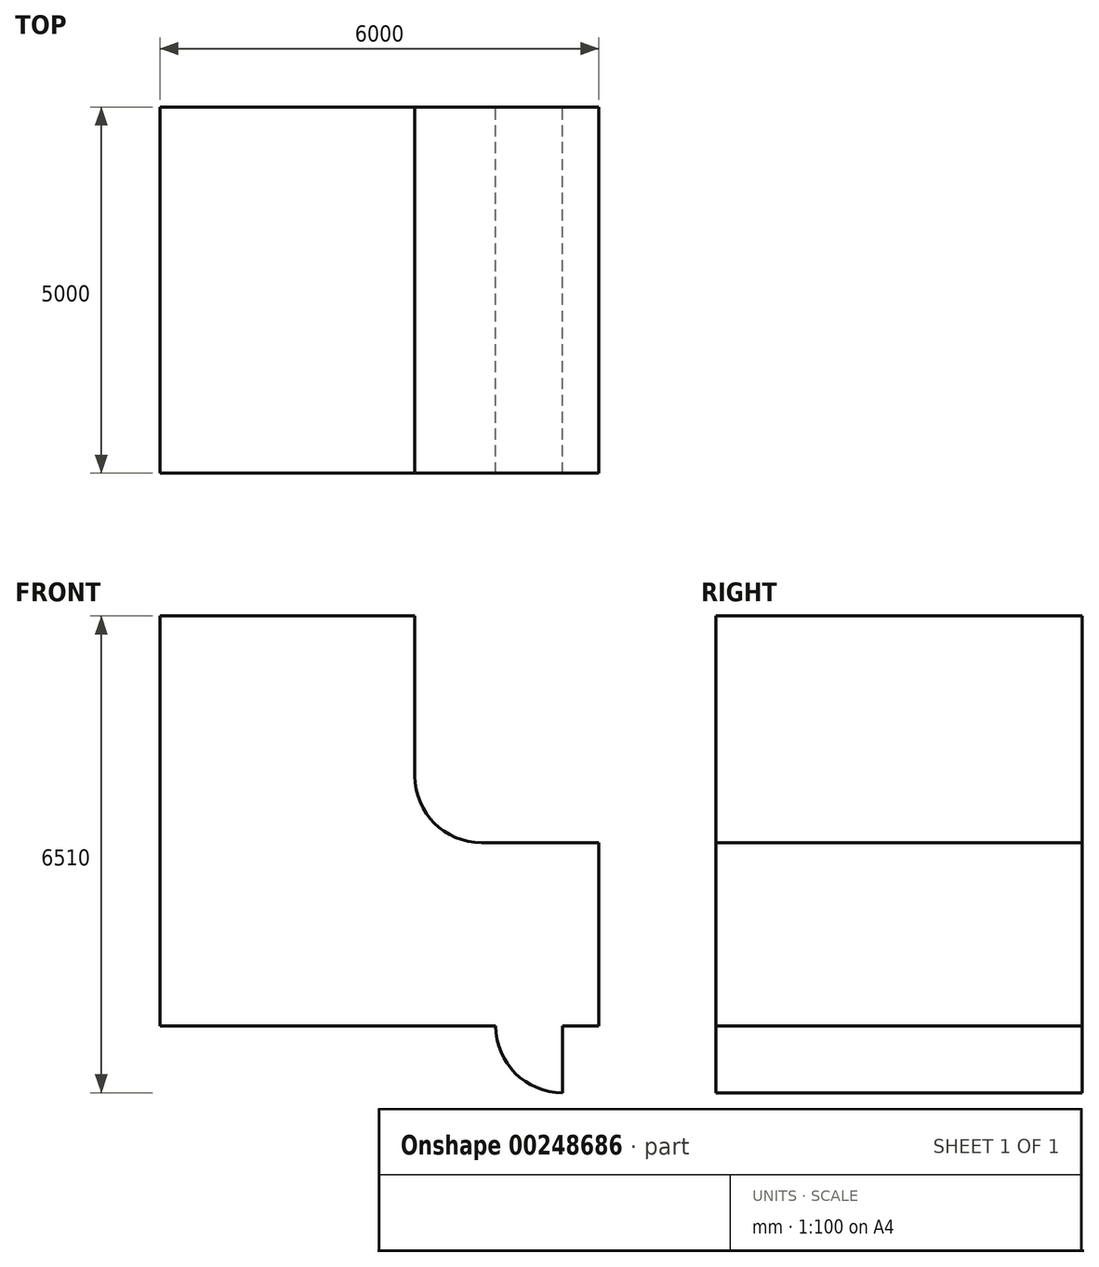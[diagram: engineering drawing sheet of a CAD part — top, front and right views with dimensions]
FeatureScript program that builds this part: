
annotation { "Feature Type Name" : "Feature", "Feature Type Description" : "" }
export const myFeature = defineFeature(function(context is Context, id is Id, definition is map)
    precondition{}
    {
        {
            var Q0;
            Q0=qCreatedBy(makeId("Front.planeOp"),FACE);
            var sketch = newSketch(context, id + "F0", { "sketchPlane" : qUnion([Q0])});
            skLineSegment(sketch, "E0", {"start": v(0, 5600) * mm, "end": v(0, 0) * mm});
            skLineSegment(sketch, "E1", {"start": v(0, 0) * mm, "end": v(4590, 0) * mm});
            skLineSegment(sketch, "E2", {"start": v(5500, 0) * mm, "end": v(6000, 0) * mm});
            skLineSegment(sketch, "E3", {"start": v(6000, 0) * mm, "end": v(6000, 2505) * mm});
            skLineSegment(sketch, "E4", {"start": v(0, 5600) * mm, "end": v(3485, 5600) * mm});
            skPoint(sketch, "E5.visualSharp", {"position": v(3485, 2505) * mm});
            skLineSegment(sketch, "E6", {"start": v(3485, 5600) * mm, "end": v(4385, 5600) * mm});
            skLineSegment(sketch, "E7", {"start": v(3485, 5600) * mm, "end": v(3485, 3415) * mm});
            skLineSegment(sketch, "E8", {"start": v(4395, 2505) * mm, "end": v(6000, 2505) * mm});
            skLineSegment(sketch, "E9", {"start": v(3935, 5600) * mm, "end": v(3935, 3410) * mm});
            skLineSegment(sketch, "E10", {"start": v(4385, 5600) * mm, "end": v(4385, 3405) * mm});
            skLineSegment(sketch, "E11", {"start": v(4390, 2955) * mm, "end": v(6000, 2955) * mm});
            skLineSegment(sketch, "E12", {"start": v(4385, 3405) * mm, "end": v(6000, 3405) * mm});
            skLineSegment(sketch, "E13", {"start": v(6000, 3405) * mm, "end": v(6000, 2505) * mm});
            skLineSegment(sketch, "E14", {"start": v(3485, 5600) * mm, "end": v(3485, 5310) * mm});
            skLineSegment(sketch, "E15", {"start": v(3485, 5310) * mm, "end": v(3485, 5020) * mm});
            skLineSegment(sketch, "E16", {"start": v(3485, 5020) * mm, "end": v(3485, 4730) * mm});
            skLineSegment(sketch, "E17", {"start": v(3485, 4730) * mm, "end": v(3485, 4440) * mm});
            skLineSegment(sketch, "E18", {"start": v(3485, 4440) * mm, "end": v(3485, 4150) * mm});
            skLineSegment(sketch, "E19", {"start": v(3485, 4150) * mm, "end": v(3485, 3860) * mm});
            skLineSegment(sketch, "E20", {"start": v(3485, 3860) * mm, "end": v(4385, 3860) * mm});
            skLineSegment(sketch, "E21", {"start": v(3485, 4150) * mm, "end": v(4385, 4150) * mm});
            skLineSegment(sketch, "E22", {"start": v(3485, 4440) * mm, "end": v(4385, 4440) * mm});
            skLineSegment(sketch, "E23", {"start": v(4385, 4440) * mm, "end": v(4385, 4150) * mm});
            skLineSegment(sketch, "E24", {"start": v(4385, 3860) * mm, "end": v(4385, 4150) * mm});
            skLineSegment(sketch, "E25", {"start": v(3485, 4730) * mm, "end": v(4385, 4730) * mm});
            skLineSegment(sketch, "E26", {"start": v(4385, 4730) * mm, "end": v(4385, 4440) * mm});
            skLineSegment(sketch, "E27", {"start": v(3485, 5020) * mm, "end": v(4385, 5020) * mm});
            skLineSegment(sketch, "E28", {"start": v(4385, 5020) * mm, "end": v(4385, 4730) * mm});
            skLineSegment(sketch, "E29", {"start": v(3485, 5310) * mm, "end": v(4385, 5310) * mm});
            skLineSegment(sketch, "E30", {"start": v(4385, 5310) * mm, "end": v(4385, 5020) * mm});
            skLineSegment(sketch, "E31", {"start": v(4385, 5600) * mm, "end": v(4385, 5310) * mm});
            skLineSegment(sketch, "E32", {"start": v(6000, 2505) * mm, "end": v(5710, 2505) * mm});
            skLineSegment(sketch, "E33", {"start": v(5710, 2505) * mm, "end": v(5420, 2505) * mm});
            skLineSegment(sketch, "E34", {"start": v(5420, 2505) * mm, "end": v(5130, 2505) * mm});
            skLineSegment(sketch, "E35", {"start": v(5130, 2505) * mm, "end": v(4840, 2505) * mm});
            skLineSegment(sketch, "E36", {"start": v(5710, 2505) * mm, "end": v(5710, 3405) * mm});
            skLineSegment(sketch, "E37", {"start": v(5710, 3405) * mm, "end": v(6000, 3405) * mm});
            skLineSegment(sketch, "E38", {"start": v(5420, 2505) * mm, "end": v(5420, 3405) * mm});
            skLineSegment(sketch, "E39", {"start": v(5420, 3405) * mm, "end": v(5710, 3405) * mm});
            skLineSegment(sketch, "E40", {"start": v(5130, 2505) * mm, "end": v(5130, 3405) * mm});
            skLineSegment(sketch, "E41", {"start": v(5130, 3405) * mm, "end": v(5420, 3405) * mm});
            skLineSegment(sketch, "E42", {"start": v(4840, 2505) * mm, "end": v(4840, 3405) * mm});
            skLineSegment(sketch, "E43", {"start": v(4840, 3405) * mm, "end": v(5130, 3405) * mm});
            skPoint(sketch, "E44.visualSharp", {"position": v(3935, 2955) * mm});
            skArc(sketch, "E44.filletArc", {"start": v(3935, 3410) * mm, "mid": v(4068.27, 3088.27) * mm, "end": v(4390, 2955) * mm});
            skArc(sketch, "E45.filletArc", {"start": v(3485, 3415) * mm, "mid": v(3751.53, 2771.53) * mm, "end": v(4395, 2505) * mm});
            skLineSegment(sketch, "E46", {"start": v(4385, 5600) * mm, "end": v(4435, 5600) * mm});
            skLineSegment(sketch, "E47", {"start": v(4435, 5600) * mm, "end": v(4435, 3455) * mm});
            skLineSegment(sketch, "E48", {"start": v(4435, 3455) * mm, "end": v(6000, 3455) * mm});
            skLineSegment(sketch, "E49", {"start": v(6000, 3455) * mm, "end": v(6000, 3405) * mm});
            skArc(sketch, "E50", {"start": v(4590, 0) * mm, "mid": v(4856.53, -643.47) * mm, "end": v(5500, -910) * mm});
            skLineSegment(sketch, "E51", {"start": v(5500, 0) * mm, "end": v(5500, -910) * mm});
            skSolve(sketch);
        }
        {
            var Q0;
            Q0=makeQuery(id+"F0.imprint","IMPRINT",FACE,{"disambiguationData":[TD([[makeQuery(id+"F0.imprint","IMPRINT",EDGE,{"derivedFrom":sQuery(id+"F0.wireOp",EDGE,"E0")}),1.0]])]});
            extrude(context, id + "F1", {"entities" : qUnion([Q0]), "depth" : 5000 * mm});
        }
    });
